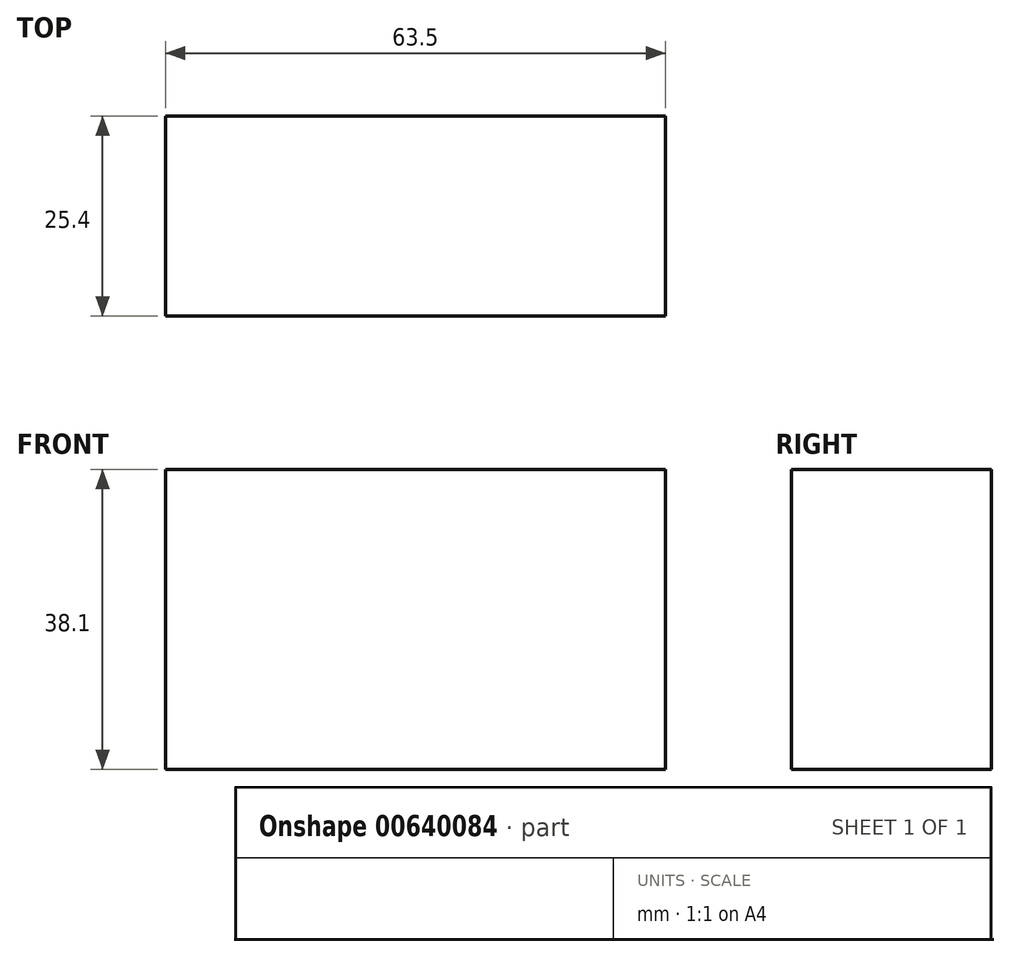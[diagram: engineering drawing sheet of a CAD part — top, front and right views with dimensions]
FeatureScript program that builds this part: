
annotation { "Feature Type Name" : "Feature", "Feature Type Description" : "" }
export const myFeature = defineFeature(function(context is Context, id is Id, definition is map)
    precondition{}
    {
        {
            var Q0;
            Q0=qCreatedBy(makeId("Top.planeOp"),FACE);
            var sketch = newSketch(context, id + "F0", { "sketchPlane" : qUnion([Q0])});
            skLineSegment(sketch, "E0", {"start": v(0, 0) * mm, "end": v(63.5, 0) * mm});
            skLineSegment(sketch, "E1", {"start": v(63.5, 0) * mm, "end": v(63.5, 25.4) * mm});
            skLineSegment(sketch, "E2", {"start": v(63.5, 25.4) * mm, "end": v(0, 25.4) * mm});
            skLineSegment(sketch, "E3", {"start": v(0, 25.4) * mm, "end": v(0, 0) * mm});
            skSolve(sketch);
        }
        {
            var Q0;
            Q0=makeQuery(id+"F0.imprint","IMPRINT",FACE,{"disambiguationData":[TD([[makeQuery(id+"F0.imprint","IMPRINT",EDGE,{"derivedFrom":sQuery(id+"F0.wireOp",EDGE,"E0")}),1.0]])]});
            extrude(context, id + "F1", {"entities" : qUnion([Q0]), "depth" : 38.1 * mm, "offsetDistance" : 25.4 * mm});
        }
    });
